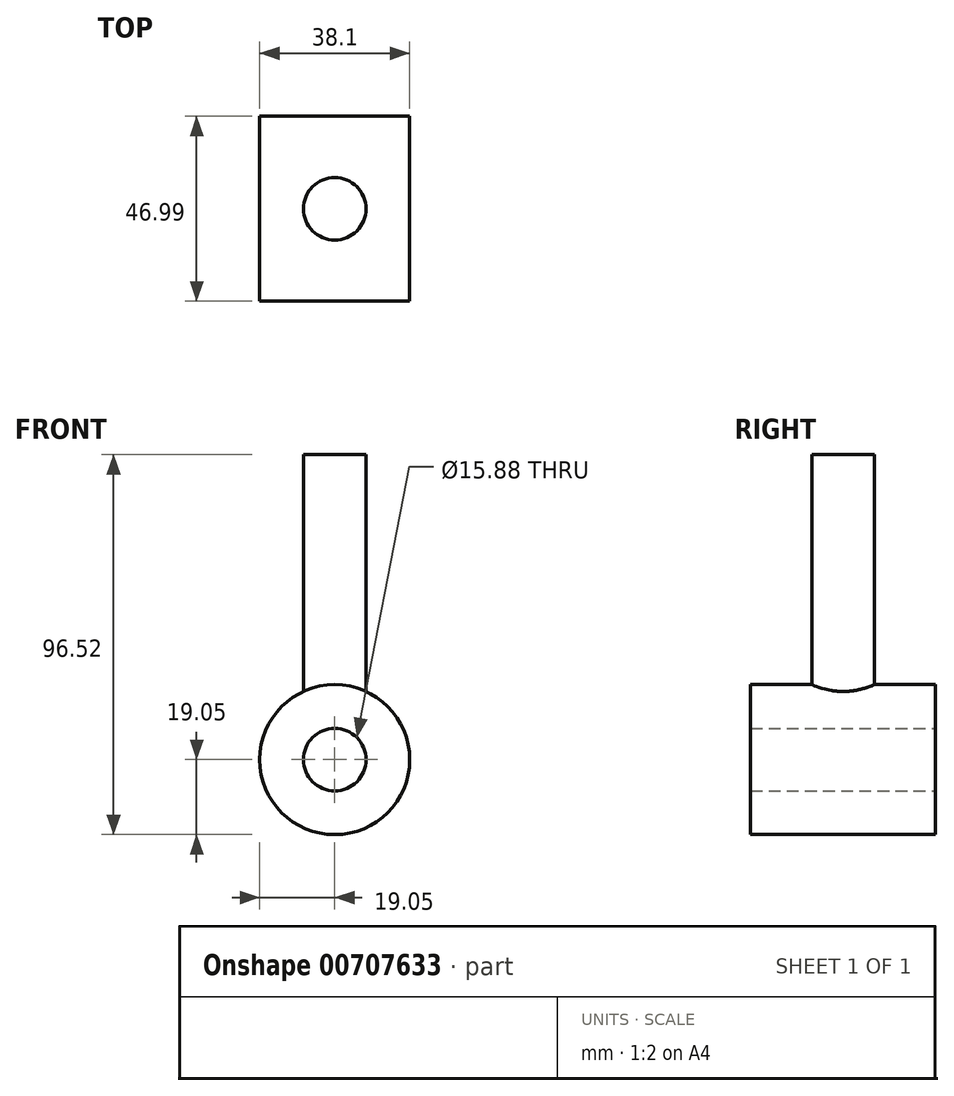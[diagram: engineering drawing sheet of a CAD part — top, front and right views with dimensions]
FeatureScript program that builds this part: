
annotation { "Feature Type Name" : "Feature", "Feature Type Description" : "" }
export const myFeature = defineFeature(function(context is Context, id is Id, definition is map)
    precondition{}
    {
        {
            var Q0;
            Q0=qCreatedBy(makeId("Front.planeOp"),FACE);
            var sketch = newSketch(context, id + "F0", { "sketchPlane" : qUnion([Q0])});
            skCircle(sketch, "E0", {"center": v(0, 0) * mm, "radius": 19.05 * mm});
            skCircle(sketch, "E1", {"center": v(0, 0) * mm, "radius": 7.94 * mm});
            skSolve(sketch);
        }
        {
            var Q0;
            Q0=qSketchRegion(id+"F0",true);
            extrude(context, id + "F1", {"entities" : qUnion([Q0]), "depth" : 47 * mm, "offsetDistance" : 25.4 * mm});
        }
        {
            var Q0;
            Q0=qCreatedBy(makeId("Top.planeOp"),FACE);
            cPlane(context, id + "F2", {"entities" : qUnion([Q0]), "cplaneType" : CPlaneType.OFFSET, "offset" : 19.05 * mm, "width" : 152.4 * mm, "height" : 152.4 * mm});
        }
        {
            var Q0;
            Q0=qCreatedBy(id+"F2.planeOp",FACE);
            var sketch = newSketch(context, id + "F3", { "sketchPlane" : qUnion([Q0])});
            skLineSegment(sketch, "E2", {"start": v(0, 0) * mm, "end": v(0, -47) * mm, "construction": true});
            skCircle(sketch, "E3", {"center": v(0, -23.5) * mm, "radius": 7.94 * mm});
            skSolve(sketch);
        }
        {
            var Q0;
            Q0=qSketchRegion(id+"F3",true);
            var Q1;
            Q1=makeQuery(id+"F1.opExtrude","SWEPT_FACE",FACE,{"disambiguationData":[OSD([sQuery(id+"F0.wireOp",EDGE,"E0")])]});
            extrude(context, id + "F4", {"entities" : qUnion([Q0]), "operationType" : NewBodyOperationType.ADD, "depth" : 58.42 * mm, "offsetDistance" : 25.4 * mm, "hasSecondDirection" : true, "secondDirectionBound" : SecondDirectionBoundingType.UP_TO_SURFACE, "secondDirectionOppositeDirection" : true, "secondDirectionDepth" : 25.4 * mm, "secondDirectionBoundEntityFace" : qUnion([Q1])});
        }
    });
